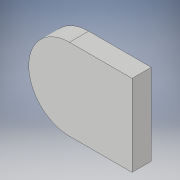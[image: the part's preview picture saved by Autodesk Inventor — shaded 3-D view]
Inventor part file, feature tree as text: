
AUTODESK INVENTOR PART (.ipt)
format: ipt  version: 2019 (Build 230136000, 136)  size: 90,624 bytes
history: native  units: in
note: dims shown in document units (in); Inventor stores cm internally (conversion verified against a paired STEP export)
features: extrude x1, sketch x1
ambient origin geometry x8: Origin, YZ Plane, XZ Plane, XY Plane, X Axis, Y Axis, Z Axis, Center Point
bodies: Solid1 (feature_tree)
feature tree (2):
  extrude  "Extrusion1"  Depth=0.1811in
  sketch  "Sketch1"  dims[d0=0.7677in d1=0.5906in d2=0.1811in d3=0.0in]
